# Revit family: ELP2_63_UN_Blank Profile_ETK
name_source: partatom
category: Lighting Fixtures
units: mm (PartAtom-declared; Revit-internal decimal feet)

## family parameters
Always vertical = No
Cut with Voids When Loaded = No
Light Source = No
OmniClass Number = 23.80.70.00
OmniClass Title = Lighting
Part Type = Normal
Room Calculation Point = Yes
Round Connector Dimension = Use Diameter
Shared = No
Work Plane-Based = No

## types (3) — shared parameters
Apparent Load = 0 VA
Assembly Code = 63.0
Description = Lightline
IfcExportAs = IfcLightFixtureType
IfcExportType = USERDEFINED
Lamp = LED
Luminaire_Body_Material = PPS Plastic
Manufacturer = ETK licht B.V.
Model = ELP2
URL = https://www.etk.nl
Voltage = 230 V
Wattage Comments = 0

## per-type parameters (varying)
| type | Length |
| 1484mm | 1484 mm  [stored 4.86877 ft] |
| 2968mm | 2968 mm  [stored 9.73753 ft] |
| 4451mm | 4451 mm  [stored 14.603 ft] |

note: [stored X ft] marks values corroborated as IEEE doubles in the binary element streams (Revit-internal decimal feet)

## geometry (parser evidence)
native form markers: Sweep x13
no freeform markers — native parametric forms only
